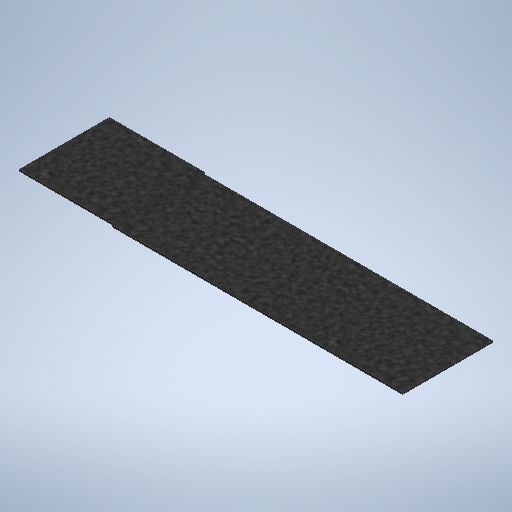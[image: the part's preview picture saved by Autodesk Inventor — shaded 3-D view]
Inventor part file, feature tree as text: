
AUTODESK INVENTOR PART (.ipt)
format: ipt  version: 2025.1 (Build 291241020, 241B)  size: 281,600 bytes
history: native  units: in
note: dims shown in document units (in); Inventor stores cm internally (conversion verified against a paired STEP export)
features: extrude x1, sketch x1
ambient origin geometry x8: Origin, YZ Plane, XZ Plane, XY Plane, X Axis, Y Axis, Z Axis, Center Point
bodies: Body1 (feature_tree)
feature tree (2):
  extrude  "Extrusion2"  Depth=0.125in
  sketch  "Sketch1"  dims[d0=6.75in d1=0.125in d2=0.125in d3=0.125in d4=0.125in d8=6.5in d9=0.0in d10=20.988in]
